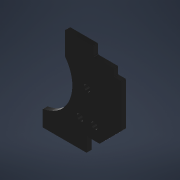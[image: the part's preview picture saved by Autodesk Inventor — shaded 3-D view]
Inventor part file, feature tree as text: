
AUTODESK INVENTOR PART (.ipt)
format: ipt  version: 2021 (Build 250183000, 183)  size: 225,792 bytes
history: native  units: mm
features: reference x8, other x5, plane x2, extrude x2, hole x1
ambient origin geometry x8: Origin, YZ Plane, XZ Plane, XY Plane, X Axis, Y Axis, Z Axis, Center Point
bodies: Solid1 (feature_tree)
feature tree (18):
  hole  "holes"  [1 undecoded]
  plane  "Work Plane1"
  extrude  "Extrusion1"  Depth=2.0mm TaperAngle=0.0deg
  plane  "Work Plane2"
  extrude  "Extrusion2"  [1 undecoded]
  reference  "Reference1"
  reference  "Reference2"
  reference  "Reference3"
  reference  "Reference4"
  reference  "Reference5"
  reference  "Reference6"
  reference  "Reference7"
  other  "plate"
  reference  "Reference8"
  other  "<userpath>\Documents\Dev\tco-cad\camera_mount\assembly_camera_mount.iam"
  other  "assembly_camera_mount.iam"
  other  "linear_stepper_carriage:1"
  other  "mount_carriage_top:1"
note: 2 required parameter values undecoded (feature->parameter linkage not recoverable at this tier; creation-order binding heuristic only, values carry confidence <= 0.55)
